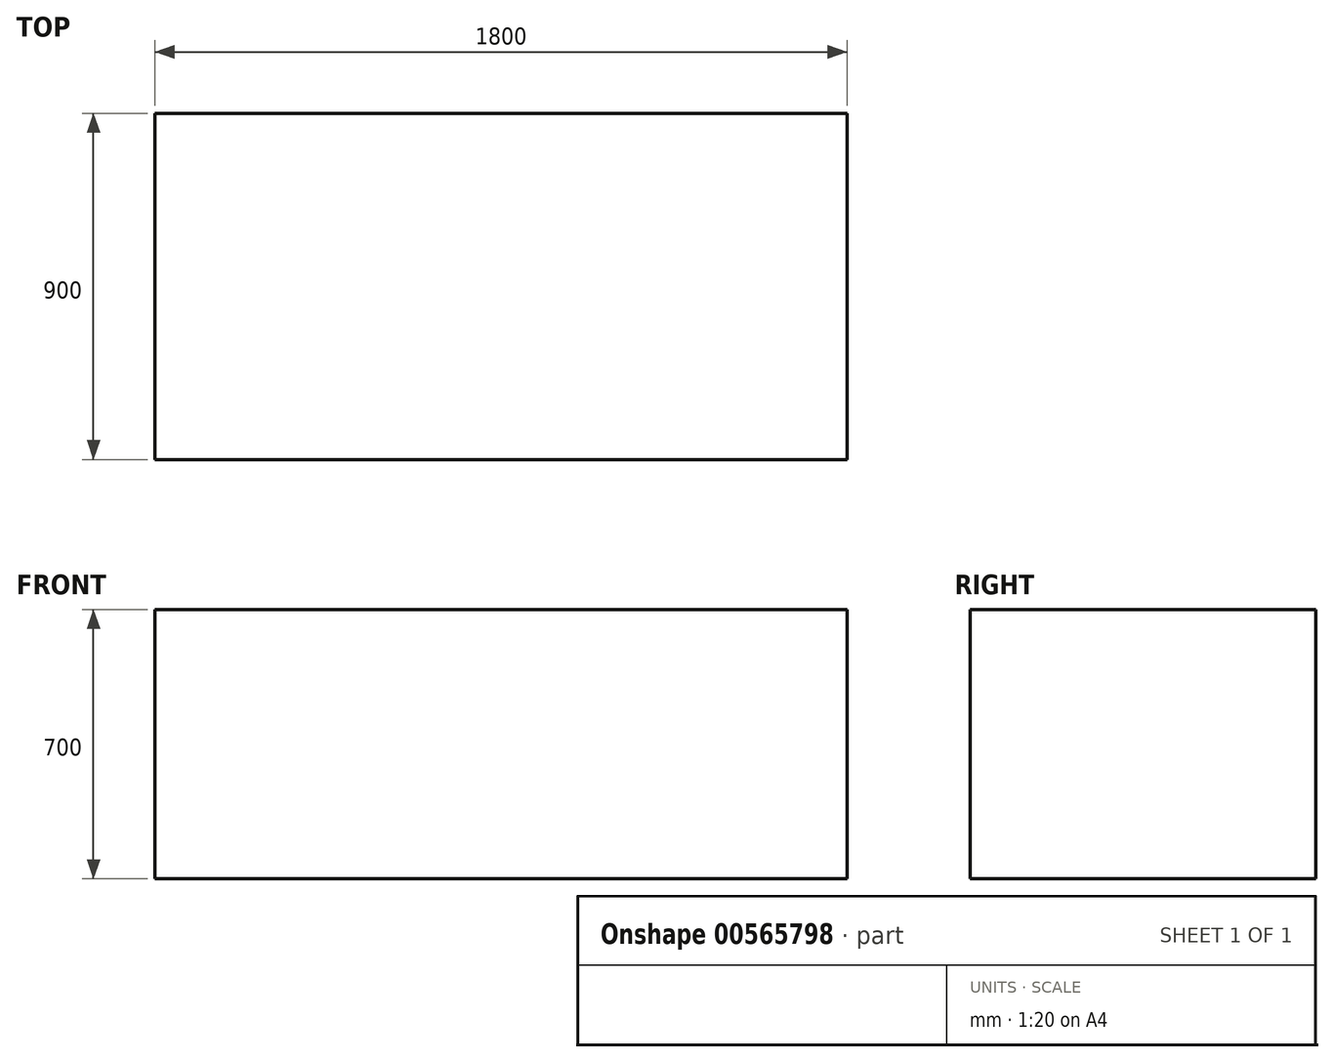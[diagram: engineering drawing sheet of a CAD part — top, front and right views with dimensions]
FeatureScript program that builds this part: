
annotation { "Feature Type Name" : "Feature", "Feature Type Description" : "" }
export const myFeature = defineFeature(function(context is Context, id is Id, definition is map)
    precondition{}
    {
        {
            var Q0;
            Q0=qCreatedBy(makeId("Top.planeOp"),FACE);
            var sketch = newSketch(context, id + "F0", { "sketchPlane" : qUnion([Q0])});
            skLineSegment(sketch, "E0.bottom", {"start": v(0, 0) * mm, "end": v(1800, 0) * mm});
            skLineSegment(sketch, "E0.top", {"start": v(0, 900) * mm, "end": v(1800, 900) * mm});
            skLineSegment(sketch, "E0.left", {"start": v(0, 0) * mm, "end": v(0, 900) * mm});
            skLineSegment(sketch, "E0.right", {"start": v(1800, 0) * mm, "end": v(1800, 900) * mm});
            skSolve(sketch);
        }
        {
            var Q0;
            Q0=makeQuery(id+"F0.imprint","IMPRINT",FACE,{"disambiguationData":[TD([[makeQuery(id+"F0.imprint","IMPRINT",EDGE,{"derivedFrom":sQuery(id+"F0.wireOp",EDGE,"E0.bottom")}),1.0]])]});
            extrude(context, id + "F1", {"entities" : qUnion([Q0]), "depth" : 700 * mm, "offsetDistance" : 25 * mm});
        }
    });
